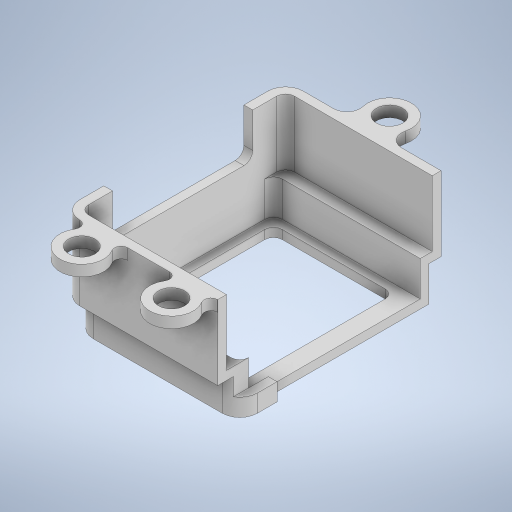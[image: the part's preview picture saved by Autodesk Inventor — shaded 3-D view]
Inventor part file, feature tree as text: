
AUTODESK INVENTOR PART (.ipt)
format: ipt  version: 2023 (Build 270158000, 158)  size: 465,920 bytes
history: native  units: in
note: dims shown in document units (in); Inventor stores cm internally (conversion verified against a paired STEP export)
features: extrude x8, sketch x4, projected_geometry x2, plane x1
ambient origin geometry x8: Origin, YZ Plane, XZ Plane, XY Plane, X Axis, Y Axis, Z Axis, Center Point
bodies: Body1 (feature_tree)
feature tree (15):
  extrude  "Extrusion3"  Depth=0.0787in
  plane  "Work Plane1"
  extrude  "Extrusion4"  Depth=0.315in TaperAngle=0.0deg
  sketch  "Sketch2"  dims[d8=0.0787in d9=0.0787in]
  extrude  "Extrusion7"  Depth=0.0787in
  extrude  "Extrusion8"  Depth=1.2402in
  extrude  "Extrusion10"  Depth=1.2402in
  extrude  "Extrusion11"  Depth=1.2402in
  extrude  "Extrusion12"  Depth=0.0787in TaperAngle=0.0deg
  extrude  "Extrusion13"  Depth=0.5906in TaperAngle=0.0deg
  projected_geometry  "Projected Loop1"
  sketch  "Sketch5"  dims[d10=0.0787in d11=0.0in d12=0.315in d13=0.0in]
  sketch  "Sketch6"  dims[d14=0.315in d19=0.0787in]
  projected_geometry  "Projected Loop3"
  sketch  "Sketch8"  dims[d20=0.0787in d21=1.2402in d22=1.2402in d23=1.2402in d28=0.0787in d29=0.0in d30=0.5906in d31=0.0in d34=0.3937in d35=0.2362in d38=0.1181in d39=0.1181in d40=0.3937in d41=0.2362in d42=0.1181in d43=0.1181in d44=0.3937in d45=0.2362in d46=0.1181in d47=0.1181in d49=0.8071in d50=0.0984in d51=0.0in d52=0.1575in d53=1.4646in d54=1.0827in d55=0.1575in d56=0.0787in d57=0.0787in d58=0.0in d59=0.0787in d61=1.2598in d62=1.6929in d64=0.2362in d65=0.0in d66=0.0787in d67=0.0787in d68=0.1772in d69=0.1575in d70=0.2362in d71=0.0in]
